# Revit family: FU_Chair_Sandler_Woodlook 2-14CB
name_source: partatom
category: Furniture
units: mm (PartAtom-declared; Revit-internal decimal feet)

## family parameters
Always vertical = Yes
Cut with Voids When Loaded = No
OmniClass Number = 23.40.20.00
OmniClass Title = General Furniture and Specialties
Room Calculation Point = No
Shared = No
Work Plane-Based = No

## types (1)
- FU_Chair_Sandler_Woodlook 2-14CB
    D = 620 mm  [stored 2.03412 ft]
    Default Elevation = 0 mm  [stored 0 ft]
    Description = Woodlook sidechair with frame manufactured entirely from aluminum but with realistic appearance of wood.
Lightweight and highly scratch resistant.
    H = 840 mm  [stored 2.75591 ft]
    Manufacturer = Sandler
    Model = Woodlook 2.14CB
    Ov-W = 595 mm  [stored 1.9521 ft]
    S-H = 480 mm  [stored 1.5748 ft]
    SW = 510 mm  [stored 1.67323 ft]
    URL = https://www.sandlerseating.com
    Upholstery = Fabric - Mainline Flax - Upminster MLF20
    Woodlook = Woodlook - 88 Grey

note: [stored X ft] marks values corroborated as IEEE doubles in the binary element streams (Revit-internal decimal feet)

## geometry (parser evidence)
native form markers: Sweep x5
no freeform markers — native parametric forms only
